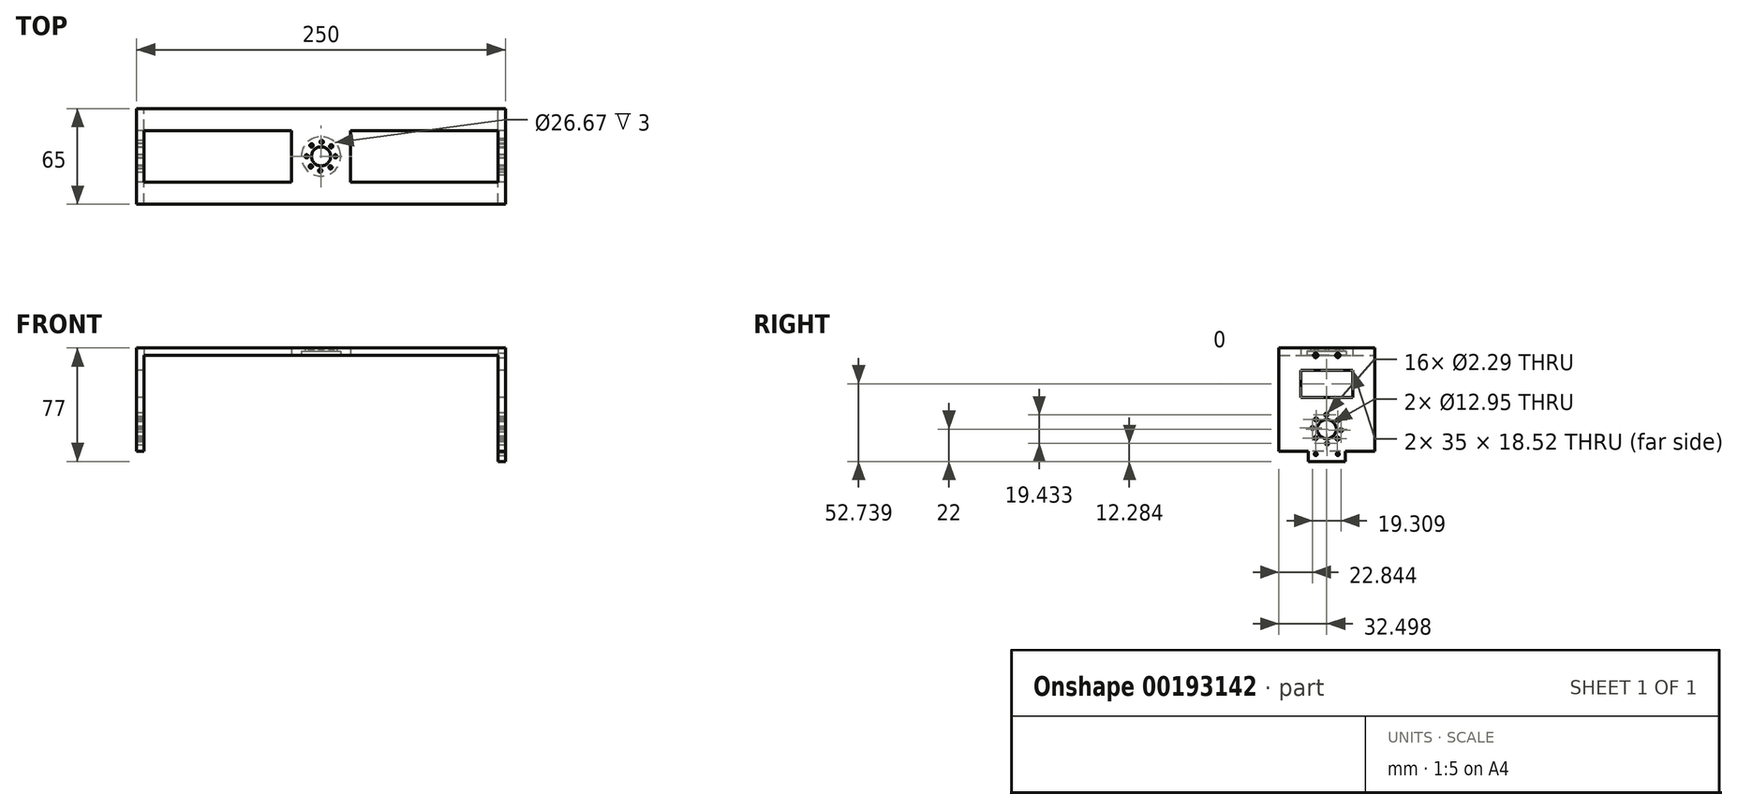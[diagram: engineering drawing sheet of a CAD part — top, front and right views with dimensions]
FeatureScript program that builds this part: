
annotation { "Feature Type Name" : "Feature", "Feature Type Description" : "" }
export const myFeature = defineFeature(function(context is Context, id is Id, definition is map)
    precondition{}
    {
        {
            var Q0;
            Q0=qCreatedBy(makeId("Top.planeOp"),FACE);
            var sketch = newSketch(context, id + "F0", { "sketchPlane" : qUnion([Q0])});
            skLineSegment(sketch, "E0.bottom", {"start": v(-116.7, 16.98) * mm, "end": v(133.3, 16.98) * mm});
            skLineSegment(sketch, "E0.top", {"start": v(-116.7, -48.02) * mm, "end": v(133.3, -48.02) * mm});
            skLineSegment(sketch, "E0.left", {"start": v(-116.7, 16.98) * mm, "end": v(-116.7, -48.02) * mm});
            skLineSegment(sketch, "E0.right", {"start": v(133.3, 16.98) * mm, "end": v(133.3, -48.02) * mm});
            skLineSegment(sketch, "E1.bottom", {"start": v(-116.7, 16.98) * mm, "end": v(-111.7, 16.98) * mm});
            skLineSegment(sketch, "E1.top", {"start": v(-116.7, -48.02) * mm, "end": v(-111.7, -48.02) * mm});
            skLineSegment(sketch, "E1.right", {"start": v(-111.7, 16.98) * mm, "end": v(-111.7, -48.02) * mm});
            skLineSegment(sketch, "E2.bottom", {"start": v(133.3, 16.98) * mm, "end": v(128.3, 16.98) * mm});
            skLineSegment(sketch, "E2.top", {"start": v(133.3, -48.02) * mm, "end": v(128.3, -48.02) * mm});
            skLineSegment(sketch, "E2.right", {"start": v(128.3, 16.98) * mm, "end": v(128.3, -48.02) * mm});
            skSolve(sketch);
        }
        {
            var Q0;
            Q0=makeQuery(id+"F0.imprint","IMPRINT",FACE,{"disambiguationData":[TD([[makeQuery(id+"F0.imprint","IMPRINT",EDGE,{"derivedFrom":sQuery(id+"F0.wireOp",EDGE,"E1.bottom")}),-1.0]])]});
            var Q1;
            Q1=makeQuery(id+"F0.imprint","IMPRINT",FACE,{"disambiguationData":[TD([[makeQuery(id+"F0.imprint","IMPRINT",EDGE,{"derivedFrom":sQuery(id+"F0.wireOp",EDGE,"E2.bottom")}),1.0]])]});
            var Q2;
            Q2=makeQuery(id+"F0.imprint","IMPRINT",FACE,{"disambiguationData":[TD([[makeQuery(id+"F0.imprint","IMPRINT",EDGE,{"derivedFrom":sQuery(id+"F0.wireOp",EDGE,"E0.bottom")}),-1.0]])]});
            extrude(context, id + "F1", {"entities" : qUnion([Q0, Q1, Q2]), "depth" : 5 * mm});
        }
        {
            var Q0;
            Q0=makeQuery(id+"F1.opExtrude","CAP_FACE",FACE,{"disambiguationData":[OSD([sQuery(id+"F0.wireOp",EDGE,"E0.bottom"),sQuery(id+"F0.wireOp",EDGE,"E0.top"),sQuery(id+"F0.wireOp",EDGE,"E1.bottom"),sQuery(id+"F0.wireOp",EDGE,"E1.top"),sQuery(id+"F0.wireOp",EDGE,"E0.left"),sQuery(id+"F0.wireOp",EDGE,"E2.bottom"),sQuery(id+"F0.wireOp",EDGE,"E2.top"),sQuery(id+"F0.wireOp",EDGE,"E0.right")])],"isStart":true});
            var sketch = newSketch(context, id + "F2", { "sketchPlane" : qUnion([Q0])});
            skLineSegment(sketch, "E3.bottom", {"start": v(-116.7, 48.02) * mm, "end": v(-111.7, 48.02) * mm});
            skLineSegment(sketch, "E3.top", {"start": v(-116.7, -16.98) * mm, "end": v(-111.7, -16.98) * mm});
            skLineSegment(sketch, "E3.left", {"start": v(-116.7, 48.02) * mm, "end": v(-116.7, -16.98) * mm});
            skLineSegment(sketch, "E3.right", {"start": v(-111.7, 48.02) * mm, "end": v(-111.7, -16.98) * mm});
            skLineSegment(sketch, "E4.bottom", {"start": v(133.3, 48.02) * mm, "end": v(128.3, 48.02) * mm});
            skLineSegment(sketch, "E4.top", {"start": v(133.3, -16.98) * mm, "end": v(128.3, -16.98) * mm});
            skLineSegment(sketch, "E4.left", {"start": v(133.3, 48.02) * mm, "end": v(133.3, -16.98) * mm});
            skLineSegment(sketch, "E4.right", {"start": v(128.3, 48.02) * mm, "end": v(128.3, -16.98) * mm});
            skSolve(sketch);
        }
        {
            var Q0;
            Q0=makeQuery(id+"F2.imprint","IMPRINT",FACE,{"disambiguationData":[TD([[makeQuery(id+"F2.imprint","IMPRINT",EDGE,{"derivedFrom":sQuery(id+"F2.wireOp",EDGE,"E3.bottom")}),-1.0]])]});
            var Q1;
            Q1=makeQuery(id+"F2.imprint","IMPRINT",FACE,{"disambiguationData":[TD([[makeQuery(id+"F2.imprint","IMPRINT",EDGE,{"derivedFrom":sQuery(id+"F2.wireOp",EDGE,"E4.bottom")}),-1.0]])]});
            extrude(context, id + "F3", {"entities" : qUnion([Q0, Q1]), "operationType" : NewBodyOperationType.ADD, "depth" : 65 * mm});
        }
        {
            var Q0;
            Q0=makeQuery(id+"F3.boolean.opBoolean","MERGE",FACE,{"derivedFrom":[makeQuery(id+"F1.opExtrude","SWEPT_FACE",FACE,{"disambiguationData":[OSD([sQuery(id+"F0.wireOp",EDGE,"E0.right")])]}),makeQuery(id+"F3.opExtrude","SWEPT_FACE",FACE,{"disambiguationData":[OSD([sQuery(id+"F2.wireOp",EDGE,"E4.left")])]})]});
            var sketch = newSketch(context, id + "F4", { "sketchPlane" : qUnion([Q0])});
            skCircle(sketch, "E5", {"center": v(-15.52, -50) * mm, "radius": 6.48 * mm});
            skSolve(sketch);
        }
        {
            var Q0;
            Q0 = qSketchRegion(id + "F4", true);
            extrude(context, id + "F5", {"entities" : qUnion([Q0]), "operationType" : NewBodyOperationType.REMOVE, "endBound" : BoundingType.THROUGH_ALL, "oppositeDirection" : true, "depth" : 25.4 * mm});
        }
        {
            var Q0;
            Q0=makeQuery(id+"F1.opExtrude","CAP_FACE",FACE,{"disambiguationData":[OSD([sQuery(id+"F0.wireOp",EDGE,"E0.bottom"),sQuery(id+"F0.wireOp",EDGE,"E0.top"),sQuery(id+"F0.wireOp",EDGE,"E1.bottom"),sQuery(id+"F0.wireOp",EDGE,"E1.top"),sQuery(id+"F0.wireOp",EDGE,"E0.left"),sQuery(id+"F0.wireOp",EDGE,"E2.bottom"),sQuery(id+"F0.wireOp",EDGE,"E2.top"),sQuery(id+"F0.wireOp",EDGE,"E0.right")])],"isStart":true});
            var sketch = newSketch(context, id + "F6", { "sketchPlane" : qUnion([Q0])});
            skCircle(sketch, "E6", {"center": v(8.3, 15.52) * mm, "radius": 6.48 * mm});
            skCircle(sketch, "E7", {"center": v(8.3, 15.52) * mm, "radius": 12.7 * mm});
            skSolve(sketch);
        }
        {
            var Q0;
            Q0=makeQuery(id+"F6.imprint","IMPRINT",FACE,{"disambiguationData":[TD([[makeQuery(id+"F6.imprint","IMPRINT",EDGE,{"derivedFrom":sQuery(id+"F6.wireOp",EDGE,"51ba74d6-f589-4a2a-b0f3-b273a8a584750.MirrorC")}),-1.0]])]});
            var Q1;
            Q1=makeQuery(id+"F6.imprint","IMPRINT",FACE,{"disambiguationData":[TD([[makeQuery(id+"F6.imprint","IMPRINT",EDGE,{"derivedFrom":sQuery(id+"F6.wireOp",EDGE,"E6")}),1.0]])]});
            var Q2;
            Q2=makeQuery(id+"F6.imprint","IMPRINT",FACE,{"disambiguationData":[TD([[makeQuery(id+"F6.imprint","IMPRINT",EDGE,{"derivedFrom":sQuery(id+"F6.wireOp",EDGE,"VHntpFtS-5Mzm-XY4i-xidT-652qaolaVIx4")}),1.0]])]});
            var Q3;
            Q3=makeQuery(id+"F6.imprint","IMPRINT",FACE,{"disambiguationData":[TD([[makeQuery(id+"F6.imprint","IMPRINT",EDGE,{"derivedFrom":sQuery(id+"F6.wireOp",EDGE,"02578dfd-1109-4855-a310-8b63019542120.MirrorC")}),-1.0]])]});
            var Q4;
            Q4=makeQuery(id+"F6.imprint","IMPRINT",FACE,{"disambiguationData":[TD([[makeQuery(id+"F6.imprint","IMPRINT",EDGE,{"derivedFrom":sQuery(id+"F6.wireOp",EDGE,"EX7Tlu1g-XRlN-CLgg-93FB-UADfUP0R1iKg")}),1.0]])]});
            extrude(context, id + "F7", {"entities" : qUnion([Q0, Q1, Q2, Q3, Q4]), "operationType" : NewBodyOperationType.REMOVE, "oppositeDirection" : true, "depth" : 25.4 * mm});
        }
        {
            var Q0;
            Q0=makeQuery(id+"F1.opExtrude","CAP_FACE",FACE,{"disambiguationData":[OSD([sQuery(id+"F0.wireOp",EDGE,"E0.bottom"),sQuery(id+"F0.wireOp",EDGE,"E0.top"),sQuery(id+"F0.wireOp",EDGE,"E1.bottom"),sQuery(id+"F0.wireOp",EDGE,"E1.top"),sQuery(id+"F0.wireOp",EDGE,"E0.left"),sQuery(id+"F0.wireOp",EDGE,"E2.bottom"),sQuery(id+"F0.wireOp",EDGE,"E2.top"),sQuery(id+"F0.wireOp",EDGE,"E0.right")])],"isStart":true});
            var sketch = newSketch(context, id + "F8", { "sketchPlane" : qUnion([Q0])});
            skLineSegment(sketch, "E8.bottom", {"start": v(-111.7, 33.02) * mm, "end": v(-11.7, 33.02) * mm});
            skLineSegment(sketch, "E8.top", {"start": v(-111.7, -1.98) * mm, "end": v(-11.7, -1.98) * mm});
            skLineSegment(sketch, "E8.right", {"start": v(-11.7, 33.02) * mm, "end": v(-11.7, -1.98) * mm});
            skLineSegment(sketch, "E9.MirrorCS", {"start": v(128.3, 33.02) * mm, "end": v(28.3, 33.02) * mm});
            skLineSegment(sketch, "E10.MirrorCS", {"start": v(28.3, 33.02) * mm, "end": v(28.3, -1.98) * mm});
            skLineSegment(sketch, "E11.MirrorCS", {"start": v(128.3, -1.98) * mm, "end": v(28.3, -1.98) * mm});
            skLineSegment(sketch, "E12.MirrorCS", {"start": v(128.3, 33.02) * mm, "end": v(128.3, -1.98) * mm});
            skLineSegment(sketch, "E13.bottom", {"start": v(-111.7, 33.02) * mm, "end": v(-101.7, 33.02) * mm});
            skLineSegment(sketch, "E13.top", {"start": v(-111.7, -1.98) * mm, "end": v(-101.7, -1.98) * mm});
            skLineSegment(sketch, "E13.left", {"start": v(-111.7, 33.02) * mm, "end": v(-111.7, -1.98) * mm});
            skLineSegment(sketch, "E13.right", {"start": v(-101.7, 33.02) * mm, "end": v(-101.7, -1.98) * mm});
            skLineSegment(sketch, "E14.MirrorCS", {"start": v(118.3, 33.02) * mm, "end": v(118.3, -1.98) * mm});
            skLineSegment(sketch, "E15.MirrorCS", {"start": v(128.3, -1.98) * mm, "end": v(118.3, -1.98) * mm});
            skLineSegment(sketch, "E16.MirrorCS", {"start": v(128.3, 33.02) * mm, "end": v(118.3, 33.02) * mm});
            skSolve(sketch);
        }
        {
            var Q0;
            Q0=makeQuery(id+"F8.imprint","IMPRINT",FACE,{"disambiguationData":[TD([[makeQuery(id+"F8.imprint","IMPRINT",EDGE,{"derivedFrom":sQuery(id+"F8.wireOp",EDGE,"E8.bottom")}),-1.0]])]});
            var Q1;
            Q1=makeQuery(id+"F8.imprint","IMPRINT",FACE,{"disambiguationData":[TD([[makeQuery(id+"F8.imprint","IMPRINT",EDGE,{"derivedFrom":sQuery(id+"F8.wireOp",EDGE,"E9.MirrorCS")}),1.0]])]});
            extrude(context, id + "F9", {"entities" : qUnion([Q0, Q1]), "operationType" : NewBodyOperationType.REMOVE, "oppositeDirection" : true, "depth" : 25.4 * mm});
        }
        {
            var Q0;
            Q0=makeQuery(id+"F9.boolean.opBoolean","MERGE",FACE,{"derivedFrom":[makeQuery(id+"F3.opExtrude","SWEPT_FACE",FACE,{"disambiguationData":[OSD([sQuery(id+"F2.wireOp",EDGE,"E3.right")])]}),makeQuery(id+"F9.opExtrude","SWEPT_FACE",FACE,{"disambiguationData":[OSD([sQuery(id+"F8.wireOp",EDGE,"E8.left")])]})]});
            var sketch = newSketch(context, id + "F10", { "sketchPlane" : qUnion([Q0])});
            skLineSegment(sketch, "E17.bottom", {"start": v(1.98, -10) * mm, "end": v(-33.02, -10) * mm});
            skLineSegment(sketch, "E17.top", {"start": v(1.98, -28.52) * mm, "end": v(-33.02, -28.52) * mm});
            skLineSegment(sketch, "E17.left", {"start": v(1.98, -10) * mm, "end": v(1.98, -28.52) * mm});
            skLineSegment(sketch, "E17.right", {"start": v(-33.02, -10) * mm, "end": v(-33.02, -28.52) * mm});
            skSolve(sketch);
        }
        {
            var Q0;
            Q0=makeQuery(id+"F10.imprint","IMPRINT",FACE,{"disambiguationData":[TD([[makeQuery(id+"F10.imprint","IMPRINT",EDGE,{"derivedFrom":sQuery(id+"F10.wireOp",EDGE,"E17.bottom")}),1.0]])]});
            extrude(context, id + "F11", {"entities" : qUnion([Q0]), "operationType" : NewBodyOperationType.REMOVE, "endBound" : BoundingType.THROUGH_ALL, "depth" : 25.4 * mm, "hasSecondDirection" : true, "secondDirectionOppositeDirection" : true, "secondDirectionDepth" : 25.4 * mm});
        }
        {
            var Q0;
            Q0=makeQuery(id+"F3.boolean.opBoolean","MERGE",FACE,{"derivedFrom":[makeQuery(id+"F1.opExtrude","SWEPT_FACE",FACE,{"disambiguationData":[OSD([sQuery(id+"F0.wireOp",EDGE,"E0.right")])]}),makeQuery(id+"F3.opExtrude","SWEPT_FACE",FACE,{"disambiguationData":[OSD([sQuery(id+"F2.wireOp",EDGE,"E4.left")])]})]});
            var sketch = newSketch(context, id + "F12", { "sketchPlane" : qUnion([Q0])});
            skCircle(sketch, "E18", {"center": v(-8.02, 0) * mm, "radius": 1.5 * mm});
            skCircle(sketch, "E19", {"center": v(-8.02, -67) * mm, "radius": 1 * mm});
            skCircle(sketch, "E20", {"center": v(-23.02, 0) * mm, "radius": 1.5 * mm});
            skCircle(sketch, "E21", {"center": v(-23.02, -67) * mm, "radius": 1 * mm});
            skPoint(sketch, "E22", {"position": v(-15.52, -50) * mm});
            skLineSegment(sketch, "E23.bottom", {"start": v(-28.02, -65) * mm, "end": v(-3.02, -65) * mm});
            skLineSegment(sketch, "E23.top", {"start": v(-28.02, -72) * mm, "end": v(-3.02, -72) * mm});
            skLineSegment(sketch, "E23.left", {"start": v(-28.02, -65) * mm, "end": v(-28.02, -72) * mm});
            skLineSegment(sketch, "E23.right", {"start": v(-3.02, -65) * mm, "end": v(-3.02, -72) * mm});
            skSolve(sketch);
        }
        {
            var Q0;
            Q0=makeQuery(id+"F12.imprint","IMPRINT",FACE,{"disambiguationData":[TD([[makeQuery(id+"F12.imprint","IMPRINT",EDGE,{"derivedFrom":sQuery(id+"F12.wireOp",EDGE,"E20")}),1.0]])]});
            var Q1;
            Q1=makeQuery(id+"F12.imprint","IMPRINT",FACE,{"disambiguationData":[TD([[makeQuery(id+"F12.imprint","IMPRINT",EDGE,{"derivedFrom":sQuery(id+"F12.wireOp",EDGE,"E18")}),1.0]])]});
            var Q2;
            Q2=makeQuery(id+"F3.opExtrude","SWEPT_FACE",FACE,{"disambiguationData":[OSD([sQuery(id+"F2.wireOp",EDGE,"E4.right")])]});
            extrude(context, id + "F13", {"entities" : qUnion([Q0, Q1]), "operationType" : NewBodyOperationType.REMOVE, "oppositeDirection" : true, "endBoundEntityFace" : qUnion([Q2]), "depth" : 25.4 * mm});
        }
        {
            var Q0;
            Q0=makeQuery(id+"F12.imprint","IMPRINT",FACE,{"disambiguationData":[TD([[makeQuery(id+"F12.imprint","IMPRINT",EDGE,{"derivedFrom":sQuery(id+"F12.wireOp",EDGE,"E19")}),-1.0]])]});
            var Q1;
            Q1=makeQuery(id+"F3.opExtrude","SWEPT_FACE",FACE,{"disambiguationData":[OSD([sQuery(id+"F2.wireOp",EDGE,"E4.right")])]});
            extrude(context, id + "F14", {"entities" : qUnion([Q0]), "operationType" : NewBodyOperationType.ADD, "endBound" : BoundingType.UP_TO_SURFACE, "oppositeDirection" : true, "endBoundEntityFace" : qUnion([Q1]), "depth" : 25.4 * mm});
        }
        {
            var Q0;
            {var subQ0=sQuery(id+"F0.wireOp",EDGE,"E2.bottom");var subQ1=sQuery(id+"F0.wireOp",EDGE,"E1.bottom");var subQ2=sQuery(id+"F0.wireOp",EDGE,"E0.bottom");var subQ3=sQuery(id+"F0.wireOp",EDGE,"E2.top");var subQ4=sQuery(id+"F0.wireOp",EDGE,"E1.top");var subQ5=sQuery(id+"F0.wireOp",EDGE,"E0.top");Q0=makeQuery(id+"F13.boolean.opBoolean","SPLIT",FACE,{"disambiguationData":[TD([makeQuery(id+"F1.opExtrude","SWEPT_FACE",FACE,{"disambiguationData":[OSD([subQ2,subQ1,subQ0])]}),makeQuery(id+"F1.opExtrude","SWEPT_FACE",FACE,{"disambiguationData":[OSD([subQ5,subQ4,subQ3])]}),makeQuery(id+"F3.opExtrude","SWEPT_FACE",FACE,{"disambiguationData":[OSD([sQuery(id+"F2.wireOp",EDGE,"E3.bottom")])]}),makeQuery(id+"F3.opExtrude","SWEPT_FACE",FACE,{"disambiguationData":[OSD([sQuery(id+"F2.wireOp",EDGE,"E3.top")])]}),makeQuery(id+"F3.opExtrude","SWEPT_FACE",FACE,{"disambiguationData":[OSD([sQuery(id+"F2.wireOp",EDGE,"E3.right")])]}),makeQuery(id+"F3.opExtrude","SWEPT_FACE",FACE,{"disambiguationData":[OSD([sQuery(id+"F2.wireOp",EDGE,"E4.bottom")])]}),makeQuery(id+"F3.opExtrude","SWEPT_FACE",FACE,{"disambiguationData":[OSD([sQuery(id+"F2.wireOp",EDGE,"E4.top")])]}),makeQuery(id+"F3.opExtrude","SWEPT_FACE",FACE,{"disambiguationData":[OSD([sQuery(id+"F2.wireOp",EDGE,"E4.right")])]}),makeQuery(id+"F7.boolean.opBoolean","COPY",FACE,{"derivedFrom":makeQuery(id+"F7.opExtrude","SWEPT_FACE",FACE,{"disambiguationData":[OSD([sQuery(id+"F6.wireOp",EDGE,"E6")])]})}),makeQuery(id+"F9.boolean.opBoolean","COPY",FACE,{"derivedFrom":makeQuery(id+"F9.opExtrude","SWEPT_FACE",FACE,{"disambiguationData":[OSD([sQuery(id+"F8.wireOp",EDGE,"E8.bottom")])]})}),makeQuery(id+"F9.boolean.opBoolean","COPY",FACE,{"derivedFrom":makeQuery(id+"F9.opExtrude","SWEPT_FACE",FACE,{"disambiguationData":[OSD([sQuery(id+"F8.wireOp",EDGE,"E8.top")])]})}),makeQuery(id+"F9.boolean.opBoolean","COPY",FACE,{"derivedFrom":makeQuery(id+"F9.opExtrude","SWEPT_FACE",FACE,{"disambiguationData":[OSD([sQuery(id+"F8.wireOp",EDGE,"E8.right")])]})}),makeQuery(id+"F9.boolean.opBoolean","COPY",FACE,{"derivedFrom":makeQuery(id+"F9.opExtrude","SWEPT_FACE",FACE,{"disambiguationData":[OSD([sQuery(id+"F8.wireOp",EDGE,"E9.MirrorCS")])]})}),makeQuery(id+"F9.boolean.opBoolean","COPY",FACE,{"derivedFrom":makeQuery(id+"F9.opExtrude","SWEPT_FACE",FACE,{"disambiguationData":[OSD([sQuery(id+"F8.wireOp",EDGE,"E10.MirrorCS")])]})}),makeQuery(id+"F9.boolean.opBoolean","COPY",FACE,{"derivedFrom":makeQuery(id+"F9.opExtrude","SWEPT_FACE",FACE,{"disambiguationData":[OSD([sQuery(id+"F8.wireOp",EDGE,"E11.MirrorCS")])]})}),makeQuery(id+"F9.boolean.opBoolean","COPY",FACE,{"derivedFrom":makeQuery(id+"F9.opExtrude","SWEPT_FACE",FACE,{"disambiguationData":[OSD([sQuery(id+"F8.wireOp",EDGE,"E13.right")])]})}),makeQuery(id+"F9.boolean.opBoolean","COPY",FACE,{"derivedFrom":makeQuery(id+"F9.opExtrude","SWEPT_FACE",FACE,{"disambiguationData":[OSD([sQuery(id+"F8.wireOp",EDGE,"E14.MirrorCS")])]})}),makeQuery(id+"F13.opExtrude","SWEPT_FACE",FACE,{"disambiguationData":[OSD([sQuery(id+"F12.wireOp",EDGE,"E18")])]}),makeQuery(id+"F13.opExtrude","SWEPT_FACE",FACE,{"disambiguationData":[OSD([sQuery(id+"F12.wireOp",EDGE,"E20")])]})])],"derivedFrom":makeQuery(id+"F1.opExtrude","CAP_FACE",FACE,{"disambiguationData":[OSD([subQ2,subQ5,subQ1,subQ4,sQuery(id+"F0.wireOp",EDGE,"E0.left"),subQ0,subQ3,sQuery(id+"F0.wireOp",EDGE,"E0.right")])],"isStart":true})});}
            var sketch = newSketch(context, id + "F15", { "sketchPlane" : qUnion([Q0])});
            skPoint(sketch, "E24", {"position": v(8.3, 15.52) * mm});
            skCircle(sketch, "E25", {"center": v(8.3, 15.52) * mm, "radius": 13.34 * mm});
            skSolve(sketch);
        }
        {
            var Q0;
            Q0=makeQuery(id+"F15.imprint","IMPRINT",FACE,{"disambiguationData":[TD([[makeQuery(id+"F15.imprint","IMPRINT",EDGE,{"derivedFrom":sQuery(id+"F15.wireOp",EDGE,"E25")}),1.0]])]});
            extrude(context, id + "F16", {"entities" : qUnion([Q0]), "operationType" : NewBodyOperationType.REMOVE, "oppositeDirection" : true, "depth" : 3 * mm});
        }
        {
            var Q0;
            Q0=makeQuery(id+"F16.boolean.opBoolean","COPY",FACE,{"derivedFrom":makeQuery(id+"F16.opExtrude","CAP_FACE",FACE,{"disambiguationData":[OSD([sQuery(id+"F6.wireOp",EDGE,"E6"),sQuery(id+"F15.wireOp",EDGE,"E25")])],"isStart":false})});
            var sketch = newSketch(context, id + "F17", { "sketchPlane" : qUnion([Q0])});
            skCircle(sketch, "E26", {"center": v(18.08, 15.52) * mm, "radius": 1.14 * mm});
            skCircle(sketch, "E27", {"center": v(14.7, 22.92) * mm, "radius": 1.14 * mm});
            skCircle(sketch, "E28", {"center": v(15.23, 8.63) * mm, "radius": 1.14 * mm});
            skCircle(sketch, "E29", {"center": v(8.8, 5.79) * mm, "radius": 1.14 * mm});
            skCircle(sketch, "E30", {"center": v(1.9, 8.12) * mm, "radius": 1.14 * mm});
            skCircle(sketch, "E31", {"center": v(-1.48, 15.52) * mm, "radius": 1.14 * mm});
            skCircle(sketch, "E32", {"center": v(1.37, 22.42) * mm, "radius": 1.14 * mm});
            skCircle(sketch, "E33", {"center": v(7.8, 25.26) * mm, "radius": 1.14 * mm});
            skPoint(sketch, "E34", {"position": v(8.3, 15.52) * mm});
            skSolve(sketch);
        }
        {
            var Q0;
            Q0=makeQuery(id+"F17.imprint","IMPRINT",FACE,{"disambiguationData":[TD([[makeQuery(id+"F17.imprint","IMPRINT",EDGE,{"derivedFrom":sQuery(id+"F17.wireOp",EDGE,"E27")}),1.0]])]});
            var Q1;
            Q1=makeQuery(id+"F17.imprint","IMPRINT",FACE,{"disambiguationData":[TD([[makeQuery(id+"F17.imprint","IMPRINT",EDGE,{"derivedFrom":sQuery(id+"F17.wireOp",EDGE,"E26")}),1.0]])]});
            var Q2;
            Q2=makeQuery(id+"F17.imprint","IMPRINT",FACE,{"disambiguationData":[TD([[makeQuery(id+"F17.imprint","IMPRINT",EDGE,{"derivedFrom":sQuery(id+"F17.wireOp",EDGE,"E28")}),1.0]])]});
            var Q3;
            Q3=makeQuery(id+"F17.imprint","IMPRINT",FACE,{"disambiguationData":[TD([[makeQuery(id+"F17.imprint","IMPRINT",EDGE,{"derivedFrom":sQuery(id+"F17.wireOp",EDGE,"E29")}),1.0]])]});
            var Q4;
            Q4=makeQuery(id+"F17.imprint","IMPRINT",FACE,{"disambiguationData":[TD([[makeQuery(id+"F17.imprint","IMPRINT",EDGE,{"derivedFrom":sQuery(id+"F17.wireOp",EDGE,"E30")}),1.0]])]});
            var Q5;
            Q5=makeQuery(id+"F17.imprint","IMPRINT",FACE,{"disambiguationData":[TD([[makeQuery(id+"F17.imprint","IMPRINT",EDGE,{"derivedFrom":sQuery(id+"F17.wireOp",EDGE,"E31")}),1.0]])]});
            var Q6;
            Q6=makeQuery(id+"F17.imprint","IMPRINT",FACE,{"disambiguationData":[TD([[makeQuery(id+"F17.imprint","IMPRINT",EDGE,{"derivedFrom":sQuery(id+"F17.wireOp",EDGE,"E32")}),1.0]])]});
            var Q7;
            Q7=makeQuery(id+"F17.imprint","IMPRINT",FACE,{"disambiguationData":[TD([[makeQuery(id+"F17.imprint","IMPRINT",EDGE,{"derivedFrom":sQuery(id+"F17.wireOp",EDGE,"E33")}),1.0]])]});
            extrude(context, id + "F18", {"entities" : qUnion([Q0, Q1, Q2, Q3, Q4, Q5, Q6, Q7]), "operationType" : NewBodyOperationType.REMOVE, "endBound" : BoundingType.THROUGH_ALL, "oppositeDirection" : true, "depth" : 25 * mm});
        }
        {
            var Q0;
            Q0=makeQuery(id+"F3.boolean.opBoolean","MERGE",FACE,{"derivedFrom":[makeQuery(id+"F1.opExtrude","SWEPT_FACE",FACE,{"disambiguationData":[OSD([sQuery(id+"F0.wireOp",EDGE,"E0.left")])]}),makeQuery(id+"F3.opExtrude","SWEPT_FACE",FACE,{"disambiguationData":[OSD([sQuery(id+"F2.wireOp",EDGE,"E3.left")])]})]});
            var sketch = newSketch(context, id + "F19", { "sketchPlane" : qUnion([Q0])});
            skCircle(sketch, "E35", {"center": v(23.11, -56.05) * mm, "radius": 1.14 * mm});
            skCircle(sketch, "E36", {"center": v(15.28, -59.72) * mm, "radius": 1.14 * mm});
            skCircle(sketch, "E37", {"center": v(8.25, -56.53) * mm, "radius": 1.14 * mm});
            skCircle(sketch, "E38", {"center": v(5.87, -50.76) * mm, "radius": 1.14 * mm});
            skCircle(sketch, "E39", {"center": v(7.93, -43.95) * mm, "radius": 1.14 * mm});
            skCircle(sketch, "E40", {"center": v(15.77, -40.28) * mm, "radius": 1.14 * mm});
            skCircle(sketch, "E41", {"center": v(22.8, -43.47) * mm, "radius": 1.14 * mm});
            skCircle(sketch, "E42", {"center": v(25.18, -49.24) * mm, "radius": 1.14 * mm});
            skPoint(sketch, "E43", {"position": v(15.52, -50) * mm});
            skSolve(sketch);
        }
        {
            var Q0;
            Q0=makeQuery(id+"F19.imprint","IMPRINT",FACE,{"disambiguationData":[TD([[makeQuery(id+"F19.imprint","IMPRINT",EDGE,{"derivedFrom":sQuery(id+"F19.wireOp",EDGE,"E40")}),1.0]])]});
            var Q1;
            Q1=makeQuery(id+"F19.imprint","IMPRINT",FACE,{"disambiguationData":[TD([[makeQuery(id+"F19.imprint","IMPRINT",EDGE,{"derivedFrom":sQuery(id+"F19.wireOp",EDGE,"E42")}),1.0]])]});
            var Q2;
            Q2=makeQuery(id+"F19.imprint","IMPRINT",FACE,{"disambiguationData":[TD([[makeQuery(id+"F19.imprint","IMPRINT",EDGE,{"derivedFrom":sQuery(id+"F19.wireOp",EDGE,"E35")}),1.0]])]});
            var Q3;
            Q3=makeQuery(id+"F19.imprint","IMPRINT",FACE,{"disambiguationData":[TD([[makeQuery(id+"F19.imprint","IMPRINT",EDGE,{"derivedFrom":sQuery(id+"F19.wireOp",EDGE,"E36")}),1.0]])]});
            var Q4;
            Q4=makeQuery(id+"F19.imprint","IMPRINT",FACE,{"disambiguationData":[TD([[makeQuery(id+"F19.imprint","IMPRINT",EDGE,{"derivedFrom":sQuery(id+"F19.wireOp",EDGE,"E37")}),1.0]])]});
            var Q5;
            Q5=makeQuery(id+"F19.imprint","IMPRINT",FACE,{"disambiguationData":[TD([[makeQuery(id+"F19.imprint","IMPRINT",EDGE,{"derivedFrom":sQuery(id+"F19.wireOp",EDGE,"E38")}),1.0]])]});
            var Q6;
            Q6=makeQuery(id+"F19.imprint","IMPRINT",FACE,{"disambiguationData":[TD([[makeQuery(id+"F19.imprint","IMPRINT",EDGE,{"derivedFrom":sQuery(id+"F19.wireOp",EDGE,"E39")}),1.0]])]});
            var Q7;
            Q7=makeQuery(id+"F19.imprint","IMPRINT",FACE,{"disambiguationData":[TD([[makeQuery(id+"F19.imprint","IMPRINT",EDGE,{"derivedFrom":sQuery(id+"F19.wireOp",EDGE,"E41")}),1.0]])]});
            extrude(context, id + "F20", {"entities" : qUnion([Q0, Q1, Q2, Q3, Q4, Q5, Q6, Q7]), "operationType" : NewBodyOperationType.REMOVE, "endBound" : BoundingType.THROUGH_ALL, "oppositeDirection" : true, "depth" : 25 * mm});
        }
    });
